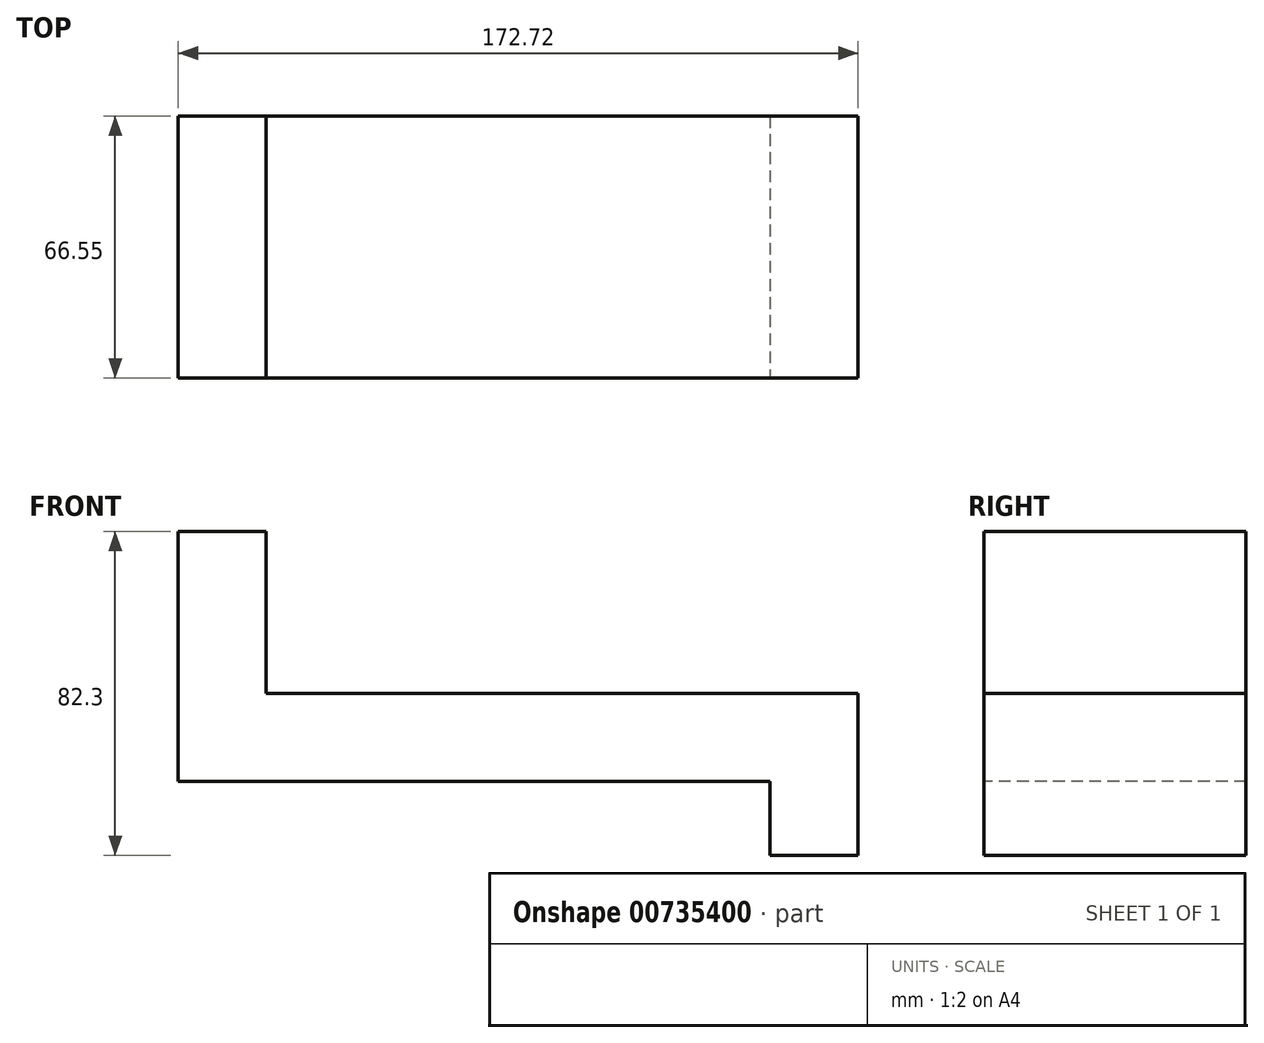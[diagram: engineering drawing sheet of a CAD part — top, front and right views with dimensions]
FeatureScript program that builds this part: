
annotation { "Feature Type Name" : "Feature", "Feature Type Description" : "" }
export const myFeature = defineFeature(function(context is Context, id is Id, definition is map)
    precondition{}
    {
        {
            var Q0;
            Q0=qCreatedBy(makeId("Front.planeOp"),FACE);
            var sketch = newSketch(context, id + "F0", { "sketchPlane" : qUnion([Q0])});
            skLineSegment(sketch, "E0", {"start": v(-65.59, 41.15) * mm, "end": v(-43.24, 41.15) * mm});
            skLineSegment(sketch, "E1", {"start": v(-43.24, 41.15) * mm, "end": v(-43.24, 0) * mm});
            skLineSegment(sketch, "E2", {"start": v(-65.59, 41.15) * mm, "end": v(-65.59, -22.35) * mm});
            skLineSegment(sketch, "E3", {"start": v(-65.59, -22.35) * mm, "end": v(84.78, -22.35) * mm});
            skLineSegment(sketch, "E4", {"start": v(-43.24, 0) * mm, "end": v(107.13, 0) * mm});
            skLineSegment(sketch, "E5", {"start": v(107.13, 0) * mm, "end": v(107.13, -41.15) * mm});
            skLineSegment(sketch, "E6", {"start": v(84.78, -22.35) * mm, "end": v(84.78, -41.08) * mm});
            skLineSegment(sketch, "E7", {"start": v(107.13, -41.15) * mm, "end": v(84.78, -41.08) * mm});
            skSolve(sketch);
        }
        {
            var Q0;
            Q0 = qSketchRegion(id + "F0", true);
            extrude(context, id + "F1", {"entities" : qUnion([Q0]), "oppositeDirection" : true, "depth" : 66.55 * mm, "offsetDistance" : 25.4 * mm});
        }
    });
